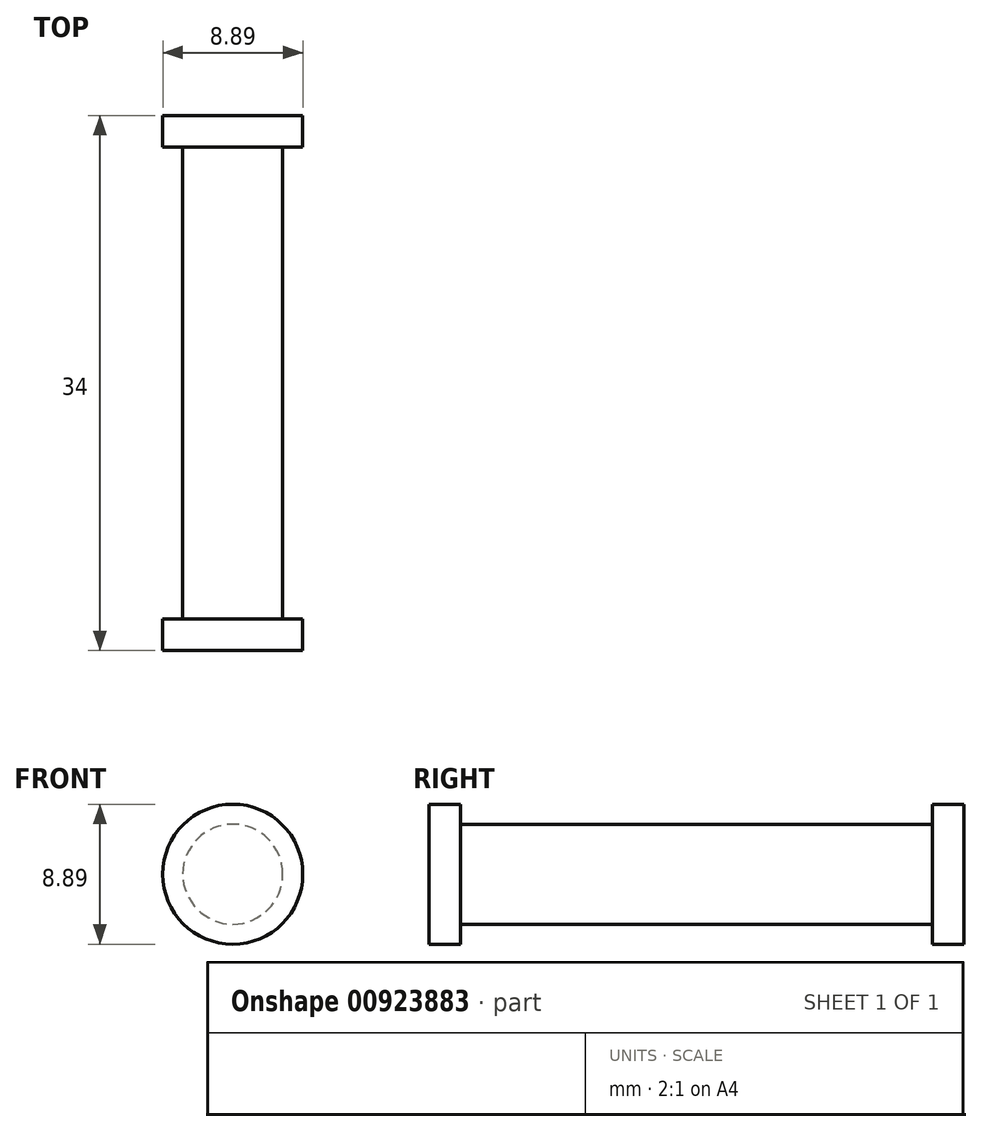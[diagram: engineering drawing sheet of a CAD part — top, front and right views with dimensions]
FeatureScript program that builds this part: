
annotation { "Feature Type Name" : "Feature", "Feature Type Description" : "" }
export const myFeature = defineFeature(function(context is Context, id is Id, definition is map)
    precondition{}
    {
        {
            var Q0;
            Q0=qCreatedBy(makeId("Front.planeOp"),FACE);
            var sketch = newSketch(context, id + "F0", { "sketchPlane" : qUnion([Q0])});
            skCircle(sketch, "E0", {"center": v(-68.06, 31.73) * mm, "radius": 3.18 * mm});
            skSolve(sketch);
        }
        {
            var Q0;
            Q0=makeQuery(id+"F0.imprint","IMPRINT",FACE,{"disambiguationData":[TD([[makeQuery(id+"F0.imprint","IMPRINT",EDGE,{"derivedFrom":sQuery(id+"F0.wireOp",EDGE,"E0")}),1.0]])]});
            extrude(context, id + "F1", {"entities" : qUnion([Q0]), "depth" : 10 * mm, "offsetDistance" : 25.4 * mm});
        }
        {
            var Q0;
            Q0=makeQuery(id+"F1.opExtrude","CAP_FACE",FACE,{"disambiguationData":[OSD([sQuery(id+"F0.wireOp",EDGE,"E0")])],"isStart":false});
            var sketch = newSketch(context, id + "F2", { "sketchPlane" : qUnion([Q0])});
            skCircle(sketch, "E1", {"center": v(-68.06, 31.73) * mm, "radius": 4.45 * mm});
            skSolve(sketch);
        }
        {
            var Q0;
            Q0=makeQuery(id+"F1.opExtrude","CAP_FACE",FACE,{"disambiguationData":[OSD([sQuery(id+"F0.wireOp",EDGE,"E0")])],"isStart":false});
            var Q1;
            Q1 = qSketchRegion(id + "F2", true);
            extrude(context, id + "F3", {"entities" : qUnion([Q0, Q1]), "operationType" : NewBodyOperationType.ADD, "depth" : 2 * mm, "offsetDistance" : 25.4 * mm});
        }
        {
            var Q0;
            Q0=makeQuery(id+"F1.opExtrude","CAP_FACE",FACE,{"disambiguationData":[OSD([sQuery(id+"F0.wireOp",EDGE,"E0")])],"isStart":true});
            extrude(context, id + "F4", {"entities" : qUnion([Q0]), "operationType" : NewBodyOperationType.ADD, "depth" : 20 * mm, "offsetDistance" : 25.4 * mm});
        }
        {
            var Q0;
            Q0=makeQuery(id+"F4.opExtrude","CAP_FACE",FACE,{"disambiguationData":[OSD([sQuery(id+"F0.wireOp",EDGE,"E0")])],"isStart":false});
            var sketch = newSketch(context, id + "F5", { "sketchPlane" : qUnion([Q0])});
            skCircle(sketch, "E2", {"center": v(68.06, 31.73) * mm, "radius": 4.45 * mm});
            skSolve(sketch);
        }
        {
            var Q0;
            Q0 = qSketchRegion(id + "F5", true);
            extrude(context, id + "F6", {"entities" : qUnion([Q0]), "operationType" : NewBodyOperationType.ADD, "depth" : 2 * mm, "offsetDistance" : 25.4 * mm});
        }
    });
